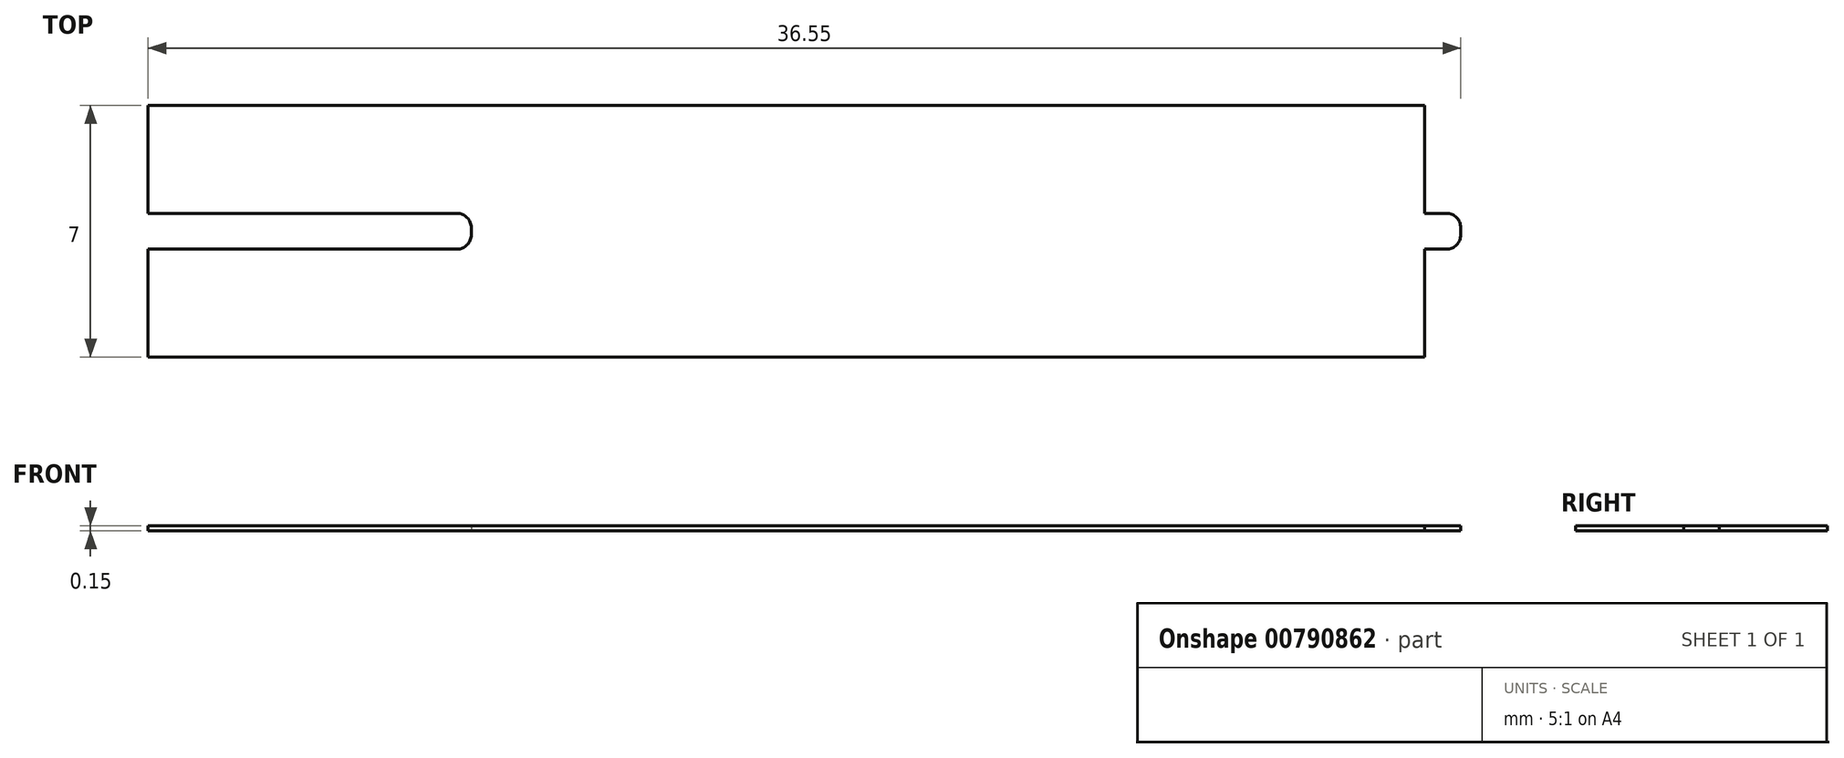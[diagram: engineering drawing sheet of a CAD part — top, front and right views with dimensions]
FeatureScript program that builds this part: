
annotation { "Feature Type Name" : "Feature", "Feature Type Description" : "" }
export const myFeature = defineFeature(function(context is Context, id is Id, definition is map)
    precondition{}
    {
        {
            var Q0;
            Q0=qCreatedBy(makeId("Top.planeOp"),FACE);
            var sketch = newSketch(context, id + "F0", { "sketchPlane" : qUnion([Q0])});
            skPoint(sketch, "E0.middle", {"position": v(0, 0) * mm});
            skLineSegment(sketch, "E1.bottom", {"start": v(-9.18, -0.5) * mm, "end": v(-13.78, -0.5) * mm});
            skLineSegment(sketch, "E1.top", {"start": v(-9.18, 0.5) * mm, "end": v(-13.78, 0.5) * mm});
            skLineSegment(sketch, "E1.left", {"start": v(-8.78, -0.1) * mm, "end": v(-8.78, 0.1) * mm});
            skLineSegment(sketch, "E1.right", {"start": v(-18.78, -0.1) * mm, "end": v(-18.78, 0.1) * mm});
            skPoint(sketch, "E1.middle", {"position": v(-13.78, 0) * mm});
            skPoint(sketch, "E2.visualSharp", {"position": v(-8.78, 0.5) * mm});
            skArc(sketch, "E2.filletArc", {"start": v(-8.78, 0.1) * mm, "mid": v(-8.9, 0.38) * mm, "end": v(-9.18, 0.5) * mm});
            skPoint(sketch, "E3.visualSharp", {"position": v(-8.78, -0.5) * mm});
            skArc(sketch, "E3.filletArc", {"start": v(-9.18, -0.5) * mm, "mid": v(-8.9, -0.38) * mm, "end": v(-8.78, -0.1) * mm});
            skPoint(sketch, "E4.visualSharp", {"position": v(-18.78, 0.5) * mm});
            skArc(sketch, "E4.filletArc", {"start": v(-18.38, 0.5) * mm, "mid": v(-18.66, 0.38) * mm, "end": v(-18.77, 0.1) * mm});
            skPoint(sketch, "E5.visualSharp", {"position": v(-18.78, -0.5) * mm});
            skArc(sketch, "E5.filletArc", {"start": v(-18.77, -0.1) * mm, "mid": v(-18.66, -0.38) * mm, "end": v(-18.38, -0.5) * mm});
            skLineSegment(sketch, "E6", {"start": v(0, 3.5) * mm, "end": v(-13.78, 3.5) * mm});
            skPoint(sketch, "E6.endSnap0", {"position": v(-13.78, 0.5) * mm});
            skLineSegment(sketch, "E7", {"start": v(-13.78, 3.5) * mm, "end": v(-13.78, 0.5) * mm});
            skLineSegment(sketch, "E8.MirrorCS", {"start": v(0, -3.5) * mm, "end": v(-13.78, -3.5) * mm});
            skLineSegment(sketch, "E9.MirrorCS", {"start": v(-13.78, -3.5) * mm, "end": v(-13.78, -0.5) * mm});
            skLineSegment(sketch, "E10.MirrorCS", {"start": v(0, 3.5) * mm, "end": v(13.78, 3.5) * mm});
            skLineSegment(sketch, "E11.MirrorCS", {"start": v(0, -3.5) * mm, "end": v(13.78, -3.5) * mm});
            skLineSegment(sketch, "E12.MirrorCS", {"start": v(8.78, -0.1) * mm, "end": v(8.78, 0.1) * mm});
            skArc(sketch, "E13.MirrorCS", {"start": v(8.78, 0.1) * mm, "mid": v(8.9, 0.38) * mm, "end": v(9.18, 0.5) * mm});
            skArc(sketch, "E14.MirrorCS", {"start": v(18.77, -0.1) * mm, "mid": v(18.66, -0.38) * mm, "end": v(18.38, -0.5) * mm});
            skLineSegment(sketch, "E15.MirrorCS", {"start": v(18.78, -0.1) * mm, "end": v(18.78, 0.1) * mm});
            skArc(sketch, "E16.MirrorCS", {"start": v(18.38, 0.5) * mm, "mid": v(18.66, 0.38) * mm, "end": v(18.77, 0.1) * mm});
            skArc(sketch, "E17.MirrorCS", {"start": v(9.18, -0.5) * mm, "mid": v(8.9, -0.38) * mm, "end": v(8.78, -0.1) * mm});
            skPoint(sketch, "E18.MirrorP", {"position": v(18.78, 0.5) * mm});
            skLineSegment(sketch, "E19.MirrorCS", {"start": v(9.18, 0.5) * mm, "end": v(18.38, 0.5) * mm});
            skLineSegment(sketch, "E20.MirrorCS", {"start": v(9.18, -0.5) * mm, "end": v(18.38, -0.5) * mm});
            skPoint(sketch, "E21.MirrorP", {"position": v(13.78, 0.5) * mm});
            skPoint(sketch, "E22.MirrorP", {"position": v(8.78, 0.5) * mm});
            skPoint(sketch, "E23.MirrorP", {"position": v(18.78, -0.5) * mm});
            skPoint(sketch, "E24.MirrorP", {"position": v(8.78, -0.5) * mm});
            skPoint(sketch, "E25.MirrorP", {"position": v(13.78, 0) * mm});
            skLineSegment(sketch, "E26.MirrorCS", {"start": v(13.78, 3.5) * mm, "end": v(13.78, 0.5) * mm});
            skLineSegment(sketch, "E27.MirrorCS", {"start": v(13.78, -3.5) * mm, "end": v(13.78, -0.5) * mm});
            skLineSegment(sketch, "E28.direction1", {"start": v(-13.78, -3.5) * mm, "end": v(13.77, -3.5) * mm, "construction": true});
            skLineSegment(sketch, "E29", {"start": v(0, 3.5) * mm, "end": v(0, -3.5) * mm});
            skLineSegment(sketch, "E30.bottom", {"start": v(-13.78, 0.5) * mm, "end": v(-17.78, 0.5) * mm});
            skLineSegment(sketch, "E30.top", {"start": v(-13.78, 3.5) * mm, "end": v(-17.78, 3.5) * mm});
            skLineSegment(sketch, "E30.left", {"start": v(-13.78, 0.5) * mm, "end": v(-13.78, 3.5) * mm});
            skLineSegment(sketch, "E30.right", {"start": v(-17.78, 0.5) * mm, "end": v(-17.78, 3.5) * mm});
            skLineSegment(sketch, "E31.bottom", {"start": v(-13.78, -3.5) * mm, "end": v(-17.78, -3.5) * mm});
            skLineSegment(sketch, "E31.top", {"start": v(-13.78, -0.5) * mm, "end": v(-17.78, -0.5) * mm});
            skLineSegment(sketch, "E31.right", {"start": v(-17.78, -3.5) * mm, "end": v(-17.78, -0.5) * mm});
            skLineSegment(sketch, "E32.MirrorCS", {"start": v(13.78, 3.5) * mm, "end": v(17.78, 3.5) * mm});
            skLineSegment(sketch, "E33.MirrorCS", {"start": v(17.78, 0.5) * mm, "end": v(17.78, 3.5) * mm});
            skLineSegment(sketch, "E34.MirrorCS", {"start": v(13.78, 0.5) * mm, "end": v(17.78, 0.5) * mm});
            skLineSegment(sketch, "E35.MirrorCS", {"start": v(13.78, -0.5) * mm, "end": v(17.78, -0.5) * mm});
            skLineSegment(sketch, "E36.MirrorCS", {"start": v(17.78, -3.5) * mm, "end": v(17.78, -0.5) * mm});
            skLineSegment(sketch, "E37.MirrorCS", {"start": v(13.78, -3.5) * mm, "end": v(17.78, -3.5) * mm});
            skSolve(sketch);
        }
        {
            var Q0;
            {var subQ8=sQuery(id+"F0.wireOp",EDGE,"E28.3.0.12");Q0=makeQuery(id+"F0.imprint","IMPRINT",FACE,{"disambiguationData":[TD([[makeQuery(id+"F0.imprint","IMPRINT",EDGE,{"derivedFrom":subQ8}),1.0]])]});}
            var Q1;
            {var subQ3=sQuery(id+"F0.wireOp",EDGE,"E14.MirrorCS");Q1=makeQuery(id+"F0.imprint","IMPRINT",FACE,{"disambiguationData":[TD([[makeQuery(id+"F0.imprint","IMPRINT",EDGE,{"derivedFrom":subQ3}),1.0]])]});}
            var Q2;
            {var subQ8=sQuery(id+"F0.wireOp",EDGE,"E28.1.0.12");Q2=makeQuery(id+"F0.imprint","IMPRINT",FACE,{"disambiguationData":[TD([[makeQuery(id+"F0.imprint","IMPRINT",EDGE,{"derivedFrom":subQ8}),1.0]])]});}
            var Q3;
            {var subQ8=sQuery(id+"F0.wireOp",EDGE,"E28.2.0.12");Q3=makeQuery(id+"F0.imprint","IMPRINT",FACE,{"disambiguationData":[TD([[makeQuery(id+"F0.imprint","IMPRINT",EDGE,{"derivedFrom":subQ8}),1.0]])]});}
            var Q4;
            Q4=makeQuery(id+"F0.imprint","IMPRINT",FACE,{"disambiguationData":[TD([[makeQuery(id+"F0.imprint","IMPRINT",EDGE,{"derivedFrom":sQuery(id+"F0.wireOp",EDGE,"E10.MirrorCS")}),-1.0]])]});
            var Q5;
            Q5=makeQuery(id+"F0.imprint","IMPRINT",FACE,{"disambiguationData":[TD([[makeQuery(id+"F0.imprint","IMPRINT",EDGE,{"derivedFrom":sQuery(id+"F0.wireOp",EDGE,"E1.bottom")}),1.0]])]});
            var Q6;
            Q6=makeQuery(id+"F0.imprint","IMPRINT",FACE,{"disambiguationData":[TD([[makeQuery(id+"F0.imprint","IMPRINT",EDGE,{"derivedFrom":sQuery(id+"F0.wireOp",EDGE,"E30.bottom")}),-1.0]])]});
            var Q7;
            Q7=makeQuery(id+"F0.imprint","IMPRINT",FACE,{"disambiguationData":[TD([[makeQuery(id+"F0.imprint","IMPRINT",EDGE,{"derivedFrom":sQuery(id+"F0.wireOp",EDGE,"E31.bottom")}),-1.0]])]});
            var Q8;
            Q8=makeQuery(id+"F0.imprint","IMPRINT",FACE,{"disambiguationData":[TD([[makeQuery(id+"F0.imprint","IMPRINT",EDGE,{"derivedFrom":sQuery(id+"F0.wireOp",EDGE,"E26.MirrorCS")}),1.0]])]});
            var Q9;
            Q9=makeQuery(id+"F0.imprint","IMPRINT",FACE,{"disambiguationData":[TD([[makeQuery(id+"F0.imprint","IMPRINT",EDGE,{"derivedFrom":sQuery(id+"F0.wireOp",EDGE,"E27.MirrorCS")}),-1.0]])]});
            extrude(context, id + "F1", {"entities" : qUnion([Q0, Q1, Q2, Q3, Q4, Q5, Q6, Q7, Q8, Q9]), "depth" : 0.15 * mm, "offsetDistance" : 25 * mm});
        }
    });
